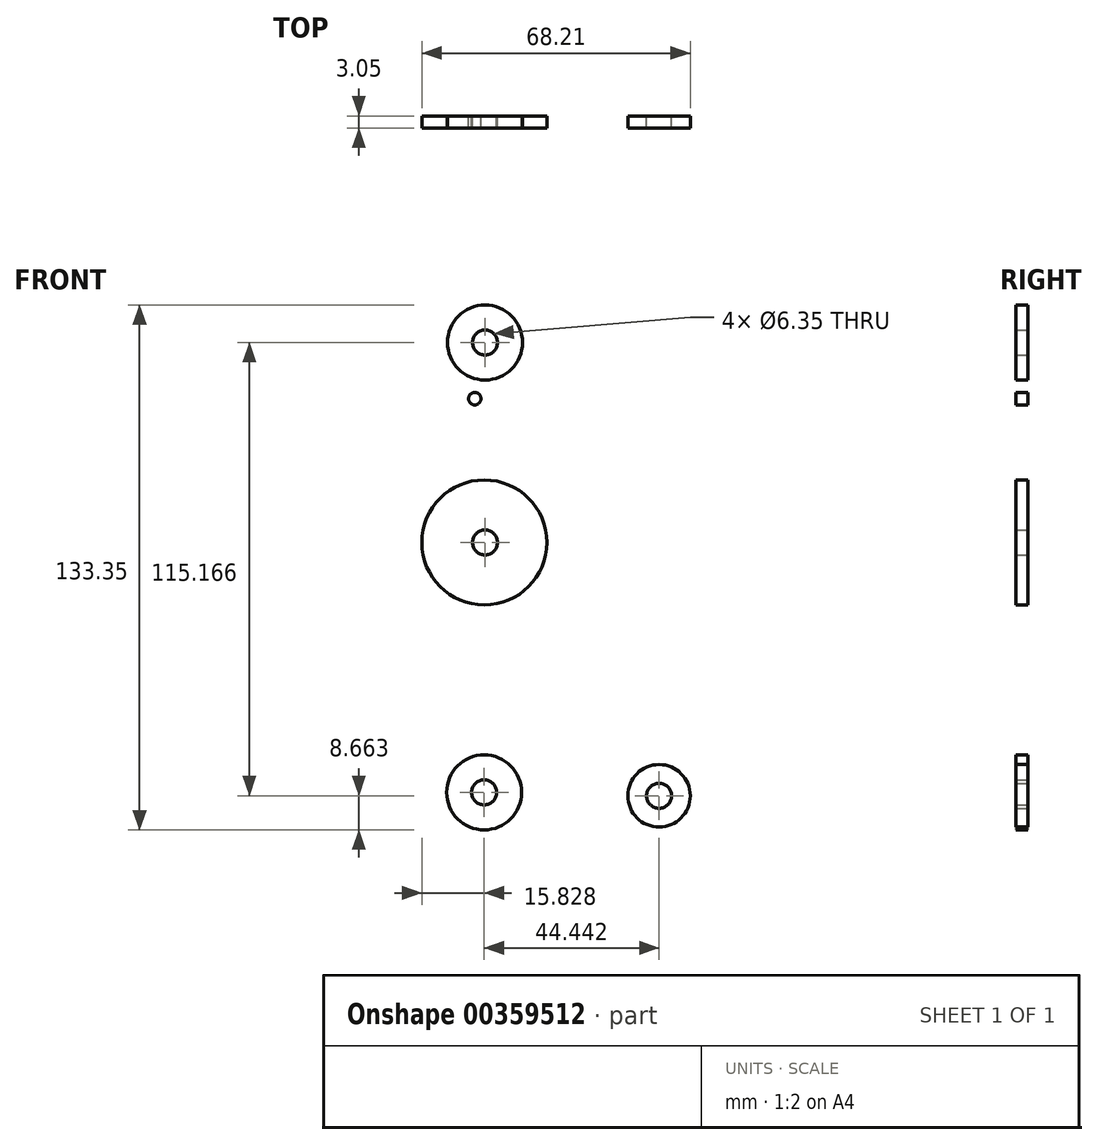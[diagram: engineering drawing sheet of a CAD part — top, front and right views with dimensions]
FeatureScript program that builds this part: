
annotation { "Feature Type Name" : "Feature", "Feature Type Description" : "" }
export const myFeature = defineFeature(function(context is Context, id is Id, definition is map)
    precondition{}
    {
        {
            var Q0;
            Q0=qCreatedBy(makeId("Front.planeOp"),FACE);
            var sketch = newSketch(context, id + "F0", { "sketchPlane" : qUnion([Q0])});
            skCircle(sketch, "E0", {"center": v(-49.03, 69.27) * mm, "radius": 9.53 * mm});
            skCircle(sketch, "E1", {"center": v(-49.2, 18.47) * mm, "radius": 15.88 * mm});
            skCircle(sketch, "E2", {"center": v(-49.24, -45.03) * mm, "radius": 9.53 * mm});
            skCircle(sketch, "E3", {"center": v(-4.8, -45.9) * mm, "radius": 7.94 * mm});
            skLineSegment(sketch, "E4", {"start": v(-49.03, 18.47) * mm, "end": v(-49.2, 18.47) * mm});
            skLineSegment(sketch, "E5", {"start": v(-49.03, 18.47) * mm, "end": v(-49.24, -45.03) * mm, "construction": true});
            skLineSegment(sketch, "E6", {"start": v(-49.24, -45.03) * mm, "end": v(-4.8, -45.9) * mm, "construction": true});
            skLineSegment(sketch, "E7", {"start": v(-49.03, 69.27) * mm, "end": v(-49.03, 18.47) * mm, "construction": true});
            skLineSegment(sketch, "E8", {"start": v(-39.5, 68.98) * mm, "end": v(-33.33, 18.97) * mm});
            skLineSegment(sketch, "E9", {"start": v(-59.06, 69.36) * mm, "end": v(-64.96, 20.37) * mm});
            skLineSegment(sketch, "E10", {"start": v(-64.96, 16.57) * mm, "end": v(-58.8, -45.22) * mm});
            skLineSegment(sketch, "E11", {"start": v(-49.3, -54.56) * mm, "end": v(-4.36, -53.83) * mm});
            skLineSegment(sketch, "E12", {"start": v(-40.55, -41.13) * mm, "end": v(-42.49, -38.31) * mm});
            skLineSegment(sketch, "E13", {"start": v(-33.42, 16.76) * mm, "end": v(-37.92, -27.8) * mm});
            skLineSegment(sketch, "E14", {"start": v(-30.45, -36.54) * mm, "end": v(-4.36, -37.97) * mm});
            skArc(sketch, "E15.filletArc", {"start": v(-37.92, -27.8) * mm, "mid": v(-36.06, -33.77) * mm, "end": v(-30.45, -36.54) * mm});
            skCircle(sketch, "E16", {"center": v(-51.63, 55) * mm, "radius": 1.59 * mm});
            skCircle(sketch, "E17", {"center": v(-49.03, 69.27) * mm, "radius": 3.18 * mm});
            skCircle(sketch, "E18", {"center": v(-49.03, 18.47) * mm, "radius": 3.18 * mm});
            skCircle(sketch, "E19", {"center": v(-49.24, -45.03) * mm, "radius": 3.18 * mm});
            skCircle(sketch, "E20", {"center": v(-4.8, -45.9) * mm, "radius": 3.18 * mm});
            skSolve(sketch);
        }
        {
            var Q0;
            Q0 = qSketchRegion(id + "F0", true);
            extrude(context, id + "F1", {"entities" : qUnion([Q0]), "depth" : 3.05 * mm});
        }
    });
